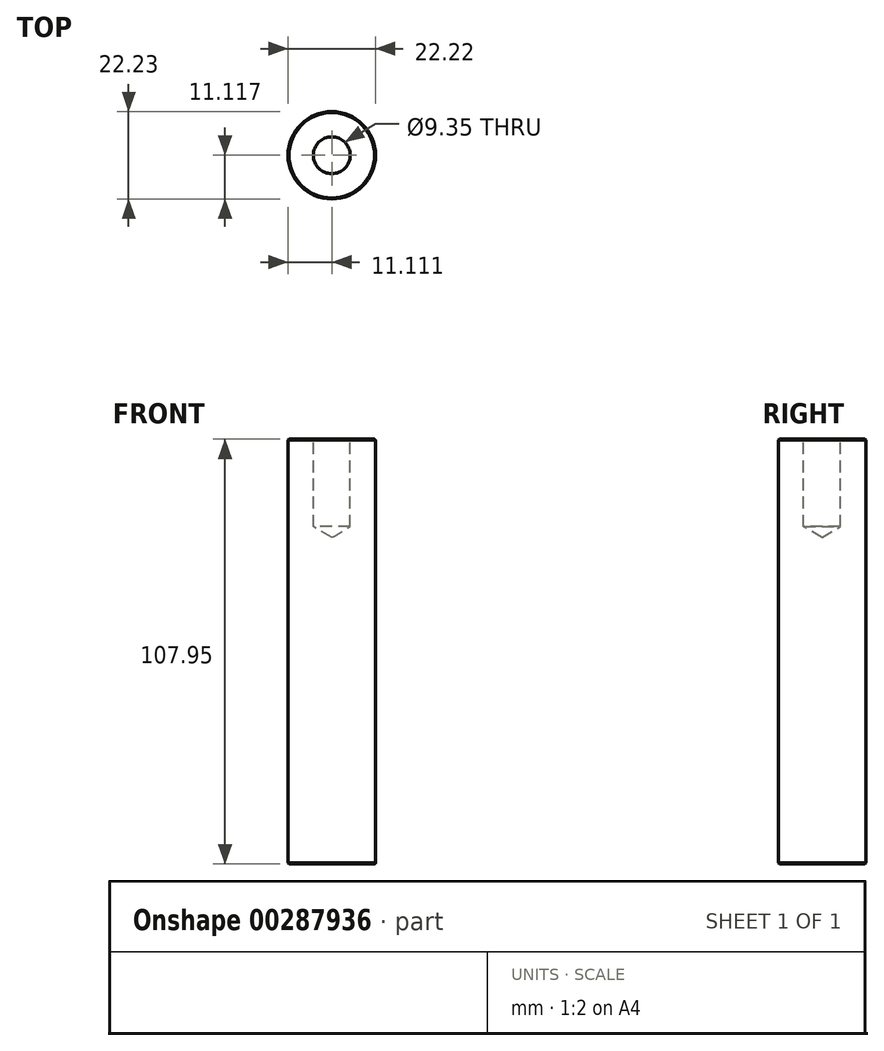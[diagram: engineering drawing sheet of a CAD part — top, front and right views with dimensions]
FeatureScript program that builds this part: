
annotation { "Feature Type Name" : "Feature", "Feature Type Description" : "" }
export const myFeature = defineFeature(function(context is Context, id is Id, definition is map)
    precondition{}
    {
        {
            var Q0;
            Q0=qCreatedBy(makeId("Top.planeOp"),FACE);
            var sketch = newSketch(context, id + "F0", { "sketchPlane" : qUnion([Q0])});
            skCircle(sketch, "E0", {"center": v(-52.52, 28.48) * mm, "radius": 11.11 * mm});
            skSolve(sketch);
        }
        {
            var Q0;
            Q0=makeQuery(id+"F0.imprint","IMPRINT",FACE,{"disambiguationData":[TD([[makeQuery(id+"F0.imprint","IMPRINT",EDGE,{"derivedFrom":sQuery(id+"F0.wireOp",EDGE,"E0")}),1.0]])]});
            extrude(context, id + "F1", {"entities" : qUnion([Q0]), "oppositeDirection" : true, "depth" : 107.95 * mm, "offsetDistance" : 25.4 * mm});
        }
        {
            var Q0;
            Q0=makeQuery(id+"F1.opExtrude","CAP_EDGE",EDGE,{"disambiguationData":[OSD([sQuery(id+"F0.wireOp",EDGE,"E0")])],"isStart":true});
            var Q1;
            Q1=makeQuery(id+"F1.opExtrude","CAP_EDGE",EDGE,{"disambiguationData":[OSD([sQuery(id+"F0.wireOp",EDGE,"E0")])],"isStart":false});
            chamfer(context, id + "F2", {"entities" : qUnion([Q0, Q1]), "chamferType" : ChamferType.OFFSET_ANGLE, "width" : 0.25 * mm, "oppositeDirection" : false, "angle" : 45 * degree, "tangentPropagation" : true});
        }
        {
            var Q0;
            Q0=sQuery(id+"F0.wireOp",VERTEX,"E0.center");
            var Q1;
            Q1=makeQuery(id+"F1.opExtrude","SWEPT_BODY",BODY,{"disambiguationData":[OSD([sQuery(id+"F0.wireOp",EDGE,"E0")])]});
            hole(context, id + "F3", {"style" : HoleStyle.SIMPLE, "endStyle" : HoleEndStyle.BLIND, "standardTappedOrClearance" : lookupTablePath({ "standard" : "ANSI", "engagement" : "75%", "pitch" : "14 tpi", "size" : "7/16", "type" : "Tapped" }), "standardBlindInLast" : lookupTablePath({ "standard" : "ANSI", "engagement" : "75%", "pitch" : "14 tpi", "size" : "7/16", "type" : "Tapped" }), "holeDiameter" : 9.35 * mm, "majorDiameter" : 11.1 * mm, "showTappedDepth" : true, "holeDepth" : 22.22 * mm, "isTappedThrough" : true, "tappedDepth" : 16.78 * mm, "tapClearance" : 3, "locations" : qUnion([Q0]), "scope" : qUnion([Q1])});
        }
    });
